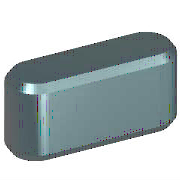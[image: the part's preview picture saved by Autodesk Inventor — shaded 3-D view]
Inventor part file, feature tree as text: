
AUTODESK INVENTOR PART (.ipt)
format: ipt  version: 2025 (Build 290162000, 162)  size: 139,776 bytes
history: native  units: mm (DEFAULTED — no unit token found)
features: plane x3, extrude x1
ambient origin geometry x8: Origin, YZ Plane, XZ Plane, XY Plane, X Axis, Y Axis, Z Axis, Center Point
bodies: Solid1 (feature_tree)
feature tree (4):
  plane  "Work Plane1"
  plane  "Work Plane2"
  extrude  "轴承体1"  Depth=6.0mm
  plane  "Work Plane3"
